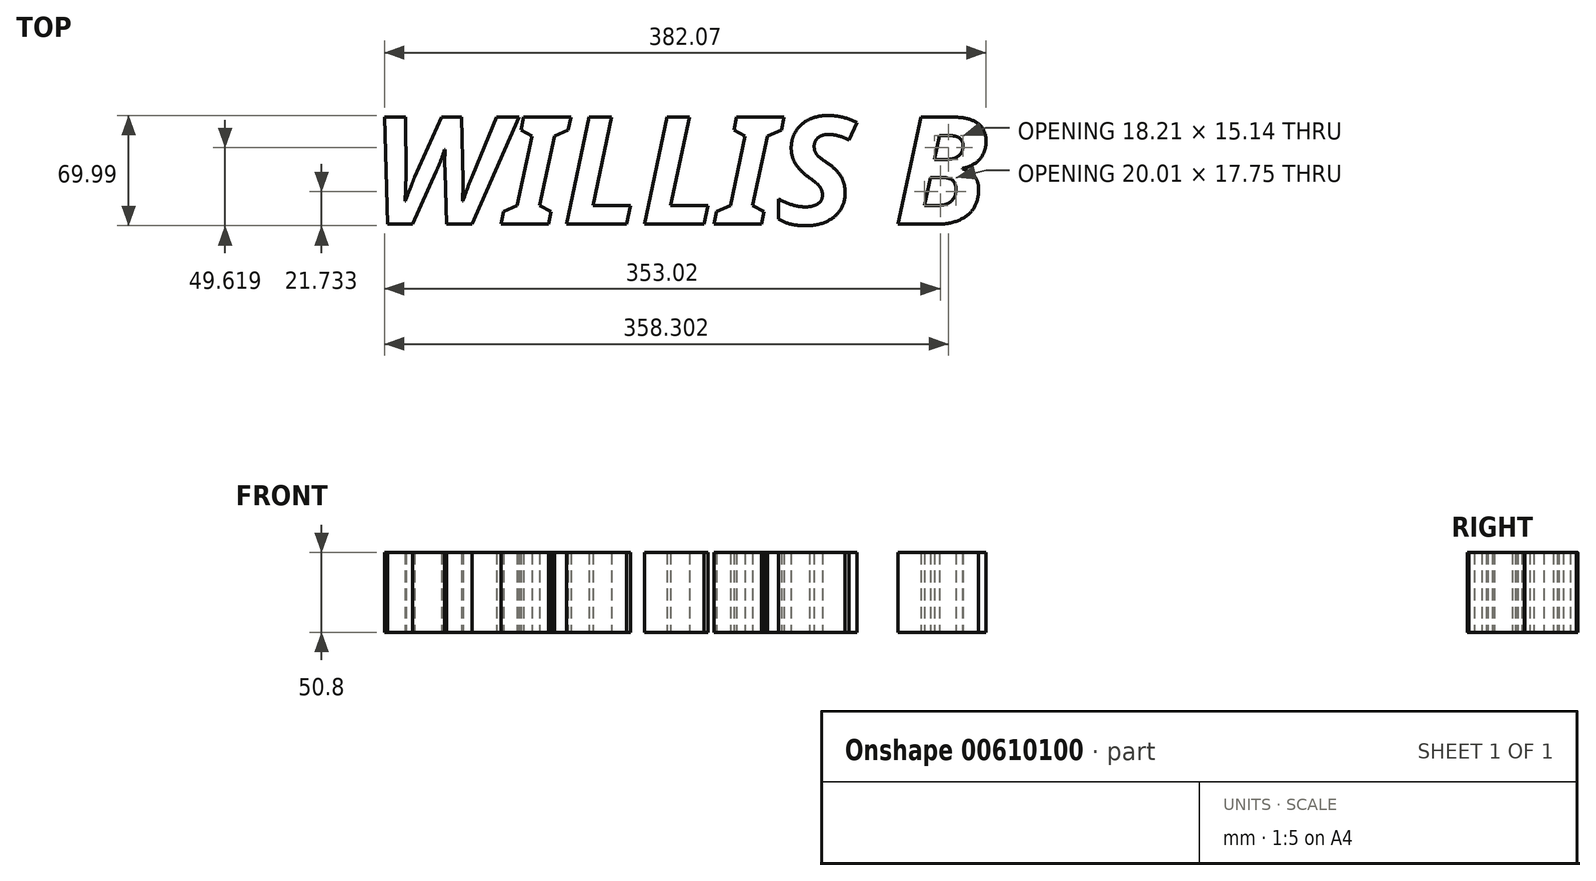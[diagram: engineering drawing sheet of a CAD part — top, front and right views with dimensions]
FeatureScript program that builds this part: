
annotation { "Feature Type Name" : "Feature", "Feature Type Description" : "" }
export const myFeature = defineFeature(function(context is Context, id is Id, definition is map)
    precondition{}
    {
        {
            var Q0;
            Q0=qCreatedBy(makeId("Top.planeOp"),FACE);
            var sketch = newSketch(context, id + "F0", { "sketchPlane" : qUnion([Q0])});
            skText(sketch, "E0", { "text": "WILLIS B", "fontName": "NotoSans-BoldItalic.ttf"});
            const initialGuessF0  = {"E0": [-0.07363, -0.0254, 1, 0, 0.06866]};
            skSetInitialGuess(sketch, initialGuessF0);
            skSolve(sketch);
        }
        {
            var Q0;
            Q0 = qSketchRegion(id + "F0", true);
            extrude(context, id + "F1", {"entities" : qUnion([Q0]), "depth" : 50.8 * mm, "offsetDistance" : 25.4 * mm});
        }
    });
